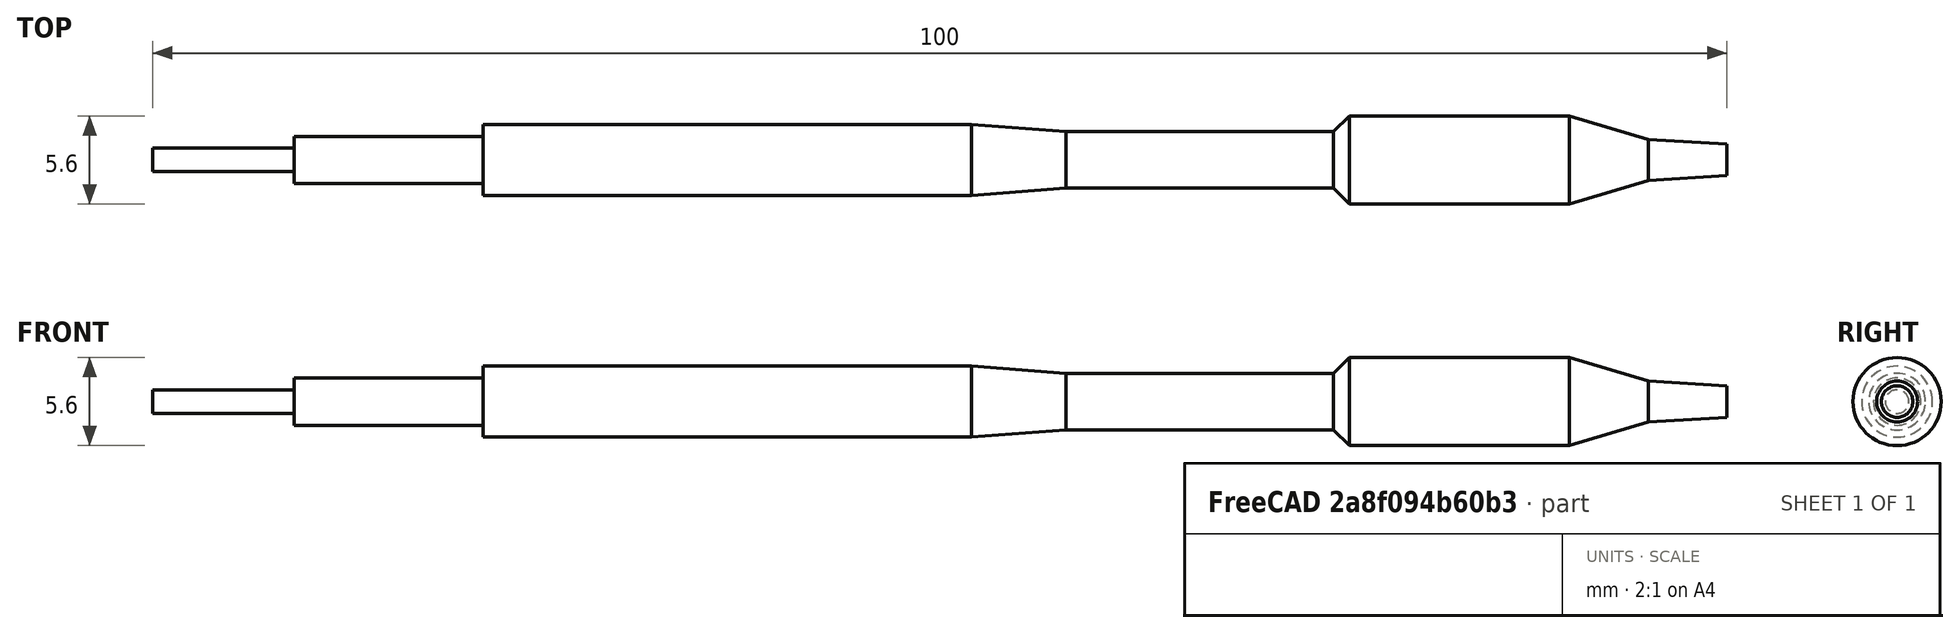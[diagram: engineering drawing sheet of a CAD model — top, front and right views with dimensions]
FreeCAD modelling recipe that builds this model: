
FCSTD DOCUMENT  (FreeCAD 0.20R28730 (Git))
Label: Tip Dummy
License: All rights reserved
LicenseURL: http://en.wikipedia.org/wiki/All_rights_reserved
objects: PartDesign::CoordinateSystem×2, Sketcher::SketchObject×1, PartDesign::Revolution×1, PartDesign::Body×1
note: 6 computed .brp shape members not serialized (recipe doc carries the construction recipe); baked Part::Feature solids carry a one-line shape summary decoded from their .brp

FEATURE [Sketcher::SketchObject] Sketch
  FullyConstrained = true
  MapMode = 5
  Placement = pos=(0,0,0) rot=(1,0,0;1.5708rad)
  Support = -> [XZ_Plane]
  sketch-geometry (14):
    g0: LineSegment StartX=0 StartY=0 StartZ=0 EndX=100 EndY=0 EndZ=0
    g1: LineSegment StartX=100 StartY=0 StartZ=0 EndX=100 EndY=1 EndZ=0
    g2: LineSegment StartX=100 StartY=1 StartZ=0 EndX=95 EndY=1.3 EndZ=0
    g3: LineSegment StartX=95 StartY=1.3 StartZ=0 EndX=90 EndY=2.8 EndZ=0
    g4: LineSegment StartX=90 StartY=2.8 StartZ=0 EndX=76 EndY=2.8 EndZ=0
    g5: LineSegment StartX=76 StartY=2.8 StartZ=0 EndX=75 EndY=1.8 EndZ=0
    g6: LineSegment StartX=75 StartY=1.8 StartZ=0 EndX=58 EndY=1.8 EndZ=0
    g7: LineSegment StartX=58 StartY=1.8 StartZ=0 EndX=52 EndY=2.25 EndZ=0
    g8: LineSegment StartX=52 StartY=2.25 StartZ=0 EndX=21 EndY=2.25 EndZ=0
    g9: LineSegment StartX=0 StartY=0 StartZ=0 EndX=0 EndY=0.75 EndZ=0
    g10: LineSegment StartX=0 StartY=0.75 StartZ=0 EndX=9 EndY=0.75 EndZ=0
    g11: LineSegment StartX=9 StartY=0.75 StartZ=0 EndX=9 EndY=1.5 EndZ=0
    g12: LineSegment StartX=9 StartY=1.5 StartZ=0 EndX=21 EndY=1.5 EndZ=0
    g13: LineSegment StartX=21 StartY=1.5 StartZ=0 EndX=21 EndY=2.25 EndZ=0
  constraints (41):
    c: Coincident(g-1,g0)
    c: PointOnObject(g0,g-1)
    c: Coincident(g0,g1)
    c: Vertical(g1)
    c: Coincident(g1,g2)
    c: Coincident(g2,g3)
    c: Coincident(g3,g4)
    c: Horizontal(g4)
    c: Coincident(g4,g5)
    c: Coincident(g5,g6)
    c: Horizontal(g6)
    c: Coincident(g6,g7)
    c: Coincident(g7,g8)
    c: Horizontal(g8)
    c: Coincident(g0,g9)
    c: PointOnObject(g9,g-2)
    c: Coincident(g9,g10)
    c: Horizontal(g10)
    c: Coincident(g10,g11)
    c: Coincident(g11,g12)
    c: Horizontal(g12)
    c: Coincident(g12,g13)
    c: Coincident(g8,g13)
    c: Vertical(g13)
    c: DistanceX(g0,g0) = 100
    c: DistanceX(g10,g10) = 9
    c: DistanceX(g2,g1) = 5
    c: DistanceX(g3,g1) = 10
    c: DistanceX(g5,g4) = 1
    c: DistanceX(g0,g7) = 52
    c: DistanceX(g0,g6) = 58
    c: DistanceX(g0,g5) = 75
    c: Vertical(g11)
    c: DistanceX(g12,g12) = 12
    c: DistanceY(g9,g9) = 0.75
    c: DistanceY(g0,g11) = 1.5
    c: DistanceY(g0,g8) = 2.25
    c: DistanceY(g0,g6) = 1.8
    c: DistanceY(g0,g4) = 2.8
    c: DistanceY(g1,g1) = 1
    c: DistanceY(g0,g2) = 1.3
FEATURE [PartDesign::Revolution] Revolution
  Angle = 360
  Axis = (1,0,0)
  Base = (0,0,0)
  Placement = pos=(0,0,0) rot=(1,0,0;1.5708rad)
  Profile = -> Sketch
  ReferenceAxis = -> X_Axis
  Refine = true
  Reversed = true
FEATURE [PartDesign::CoordinateSystem] Remover  label="LCS_Tip_Dummy_Tip_Remover"
  AttacherType = Attacher::AttachEngine3D
  MapMode = 11
  Placement = pos=(75,0,2e-16) rot=(0.57735,0.57735,-0.57735;4.18879rad)
  Support = -> [Revolution]
FEATURE [PartDesign::CoordinateSystem] Tip_base  label="LCS_Tip_Dummy_Base"
  AttacherType = Attacher::AttachEngine3D
  MapMode = 11
  Placement = pos=(0,0,0) rot=(0.57735,0.57735,-0.57735;4.18879rad)
  Support = -> [Revolution]
FEATURE [PartDesign::Body] Body  label="Tip_Dummy"
  Group = -> [Sketch,Revolution,Remover,Tip_base]
  Origin = -> Origin
  Tip = -> Revolution
